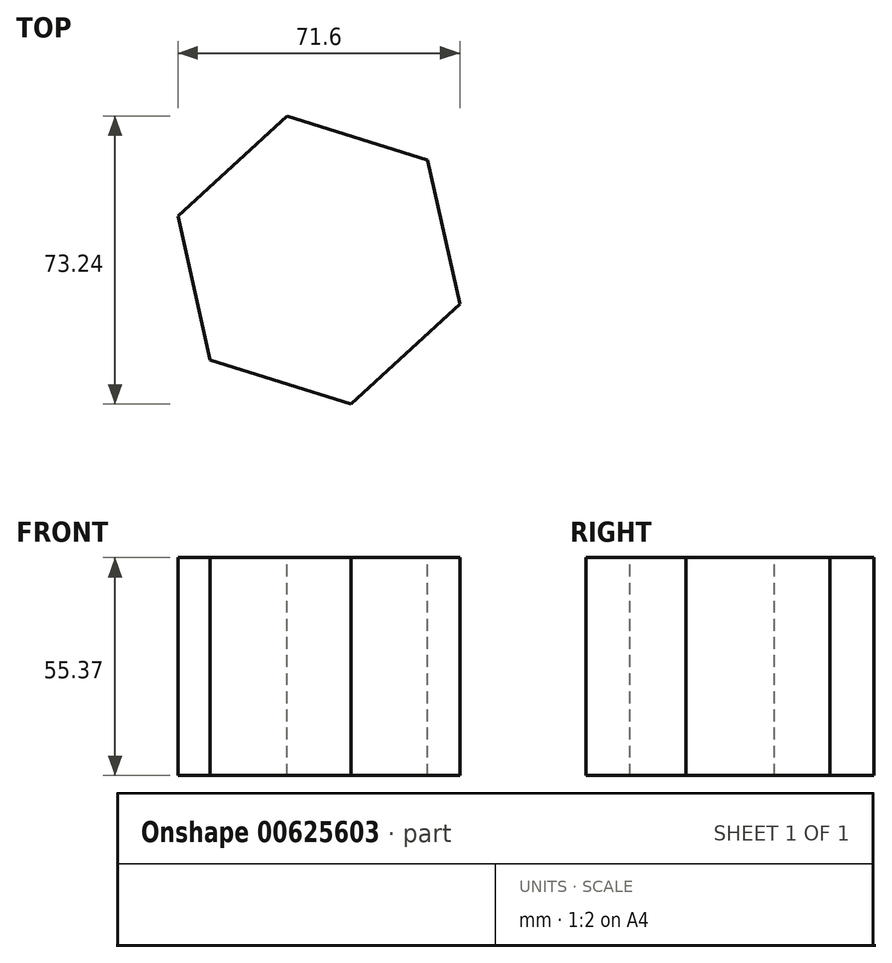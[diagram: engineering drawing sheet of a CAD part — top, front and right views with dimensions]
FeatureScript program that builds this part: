
annotation { "Feature Type Name" : "Feature", "Feature Type Description" : "" }
export const myFeature = defineFeature(function(context is Context, id is Id, definition is map)
    precondition{}
    {
        {
            var Q0;
            Q0=qCreatedBy(makeId("Top.planeOp"),FACE);
            var sketch = newSketch(context, id + "F0", { "sketchPlane" : qUnion([Q0])});
            skCircle(sketch, "E0.cCircle", {"center": v(0, 0) * mm, "radius": 32.5 * mm, "construction": true});
            skLineSegment(sketch, "E0.0", {"start": v(-35.8, 11.24) * mm, "end": v(-8.17, 36.62) * mm});
            skLineSegment(sketch, "E0.1", {"start": v(-8.17, 36.62) * mm, "end": v(27.63, 25.39) * mm});
            skLineSegment(sketch, "E0.2", {"start": v(27.63, 25.39) * mm, "end": v(35.8, -11.24) * mm});
            skLineSegment(sketch, "E0.3", {"start": v(35.8, -11.24) * mm, "end": v(8.17, -36.62) * mm});
            skLineSegment(sketch, "E0.4", {"start": v(8.17, -36.62) * mm, "end": v(-27.63, -25.39) * mm});
            skLineSegment(sketch, "E0.5", {"start": v(-27.63, -25.39) * mm, "end": v(-35.8, 11.24) * mm});
            skPoint(sketch, "E0.0.midPoint", {"position": v(-21.99, 23.93) * mm});
            skSolve(sketch);
        }
        {
            var Q0;
            Q0=makeQuery(id+"F0.imprint","IMPRINT",FACE,{"disambiguationData":[TD([[makeQuery(id+"F0.imprint","IMPRINT",EDGE,{"derivedFrom":sQuery(id+"F0.wireOp",EDGE,"E0.0")}),-1.0]])]});
            extrude(context, id + "F1", {"entities" : qUnion([Q0]), "oppositeDirection" : true, "depth" : 55.37 * mm, "offsetDistance" : 25.4 * mm});
        }
    });
